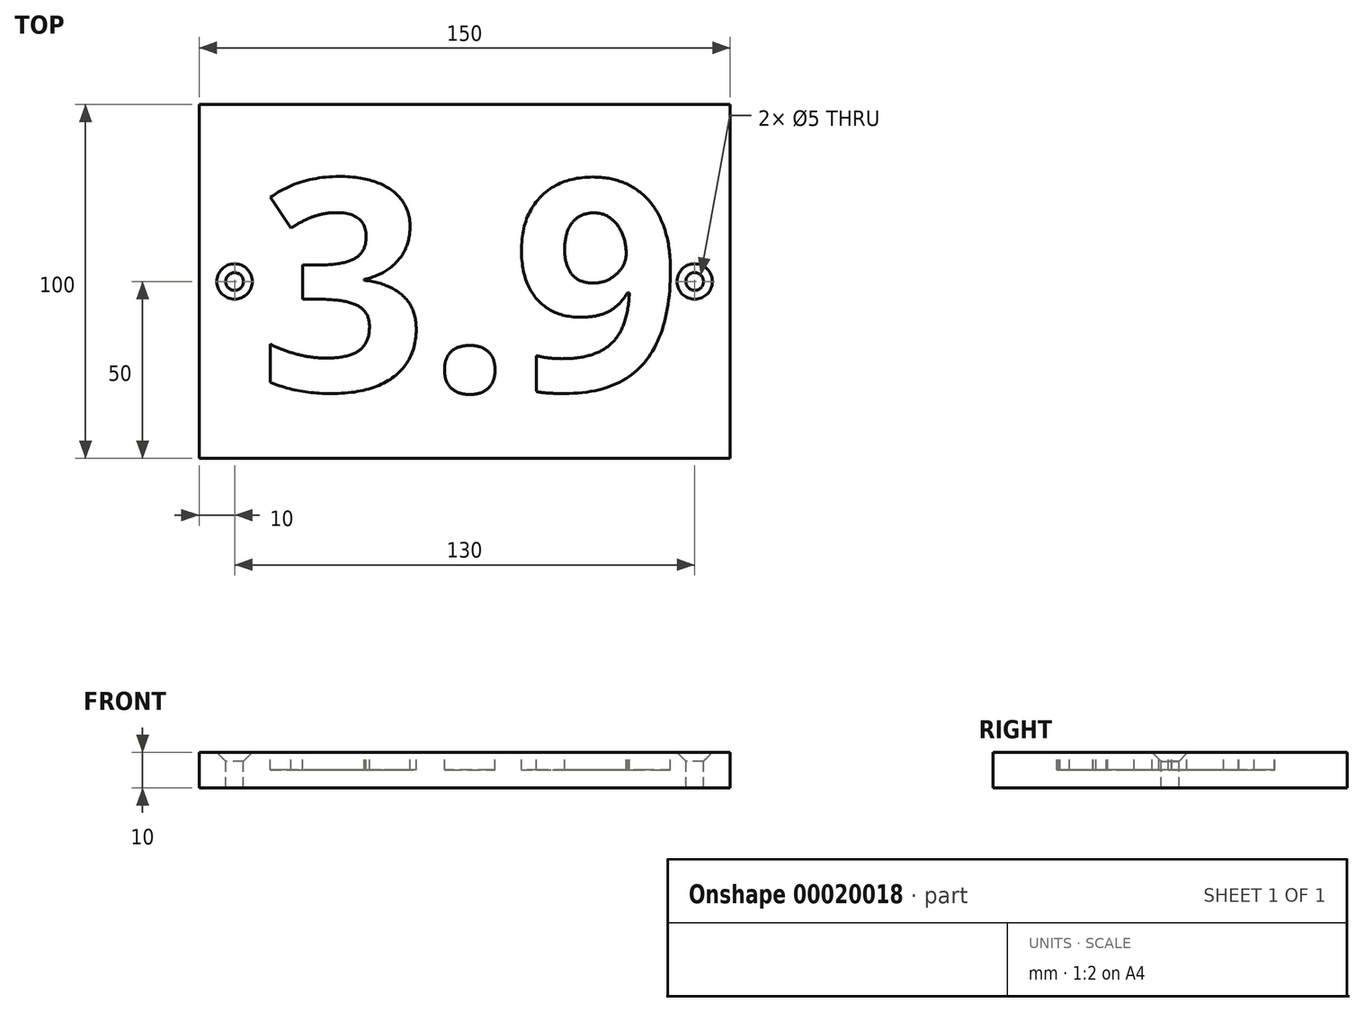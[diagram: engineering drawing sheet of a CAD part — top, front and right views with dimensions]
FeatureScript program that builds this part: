
annotation { "Feature Type Name" : "Feature", "Feature Type Description" : "" }
export const myFeature = defineFeature(function(context is Context, id is Id, definition is map)
    precondition{}
    {
        {
            var Q0;
            Q0=qCreatedBy(makeId("Top.planeOp"),FACE);
            var sketch = newSketch(context, id + "F0", { "sketchPlane" : qUnion([Q0])});
            skLineSegment(sketch, "E0.bottom", {"start": v(0, 0) * mm, "end": v(150, 0) * mm});
            skLineSegment(sketch, "E0.top", {"start": v(0, 100) * mm, "end": v(150, 100) * mm});
            skLineSegment(sketch, "E0.left", {"start": v(0, 0) * mm, "end": v(0, 100) * mm});
            skLineSegment(sketch, "E0.right", {"start": v(150, 0) * mm, "end": v(150, 100) * mm});
            skSolve(sketch);
        }
        {
            var Q0;
            Q0 = qSketchRegion(id + "F0", true);
            extrude(context, id + "F1", {"entities" : qUnion([Q0]), "depth" : 10 * mm});
        }
        {
            var Q0;
            Q0=makeQuery(id+"F1.opExtrude","CAP_FACE",FACE,{"disambiguationData":[OSD([sQuery(id+"F0.wireOp",EDGE,"E0.bottom"),sQuery(id+"F0.wireOp",EDGE,"E0.top"),sQuery(id+"F0.wireOp",EDGE,"E0.left"),sQuery(id+"F0.wireOp",EDGE,"E0.right")])],"isStart":false});
            var sketch = newSketch(context, id + "F2", { "sketchPlane" : qUnion([Q0])});
            skPoint(sketch, "E1", {"position": v(10, 50) * mm});
            skPoint(sketch, "E2", {"position": v(140, 50) * mm});
            skSolve(sketch);
        }
        {
            var Q0;
            Q0=sQuery(id+"F2.wireOp",VERTEX,"E1");
            var Q1;
            Q1=sQuery(id+"F2.wireOp",VERTEX,"E2");
            var Q2;
            Q2=makeQuery(id+"F1.opExtrude","SWEPT_BODY",BODY,{"disambiguationData":[OSD([sQuery(id+"F0.wireOp",EDGE,"E0.bottom"),sQuery(id+"F0.wireOp",EDGE,"E0.top"),sQuery(id+"F0.wireOp",EDGE,"E0.left"),sQuery(id+"F0.wireOp",EDGE,"E0.right")])]});
            hole(context, id + "F3", {"style" : HoleStyle.C_SINK, "holeDiameter" : 5 * mm, "cSinkDiameter" : 10 * mm, "endStyle" : HoleEndStyle.THROUGH, "locations" : qUnion([Q0, Q1]), "scope" : qUnion([Q2]), "cSinkAngle" : 90 * degree});
        }
        {
            var Q0;
            Q0=makeQuery(id+"F1.opExtrude","CAP_FACE",FACE,{"disambiguationData":[OSD([sQuery(id+"F0.wireOp",EDGE,"E0.bottom"),sQuery(id+"F0.wireOp",EDGE,"E0.top"),sQuery(id+"F0.wireOp",EDGE,"E0.left"),sQuery(id+"F0.wireOp",EDGE,"E0.right")])],"isStart":false});
            var sketch = newSketch(context, id + "F4", { "sketchPlane" : qUnion([Q0])});
            skText(sketch, "E3", { "text": "3.9", "fontName": "OpenSans-Bold.ttf"});
            skLineSegment(sketch, "E4", {"start": v(75, 100) * mm, "end": v(75, 0) * mm, "construction": true});
            const initialGuessF4  = {"E3": [0.01686, 0.01917, 1, 0, 0.06015]};
            skSetInitialGuess(sketch, initialGuessF4);
            skSolve(sketch);
        }
        {
            var Q0;
            Q0 = qSketchRegion(id + "F4", true);
            extrude(context, id + "F5", {"entities" : qUnion([Q0]), "operationType" : NewBodyOperationType.REMOVE, "oppositeDirection" : true, "depth" : 5 * mm});
        }
    });
